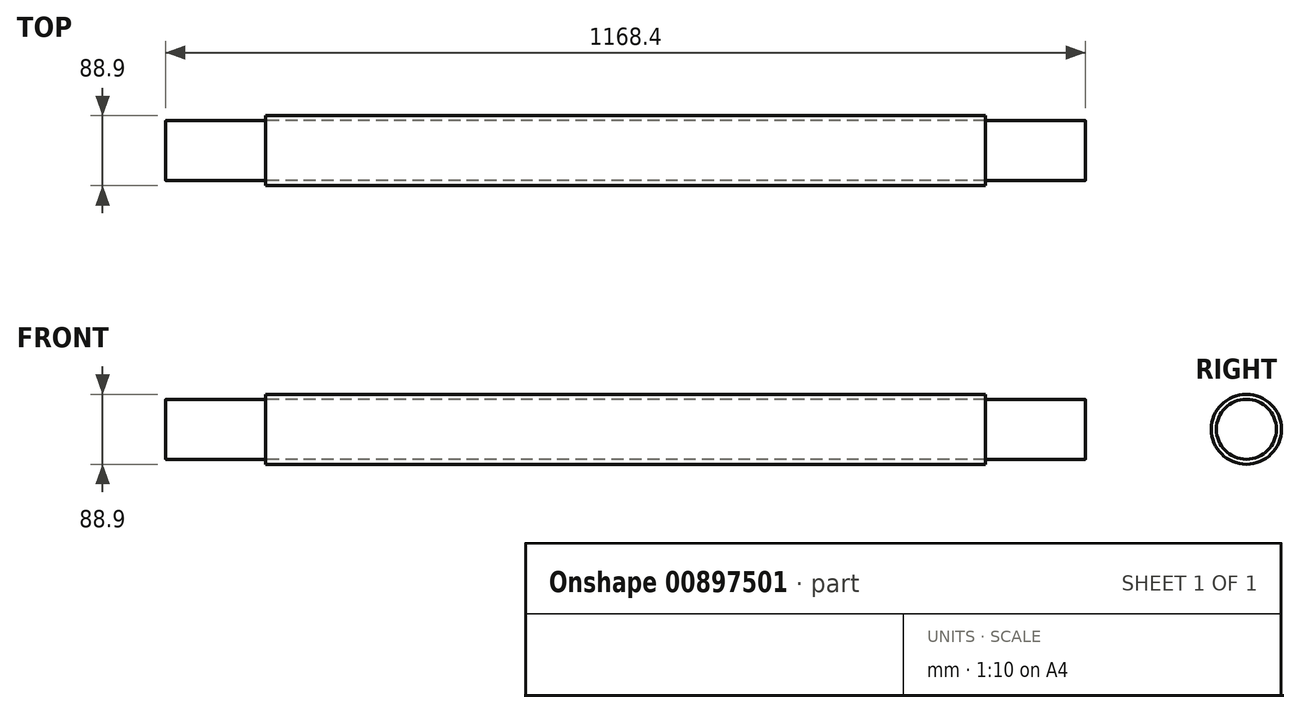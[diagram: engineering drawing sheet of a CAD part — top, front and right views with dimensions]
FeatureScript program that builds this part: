
annotation { "Feature Type Name" : "Feature", "Feature Type Description" : "" }
export const myFeature = defineFeature(function(context is Context, id is Id, definition is map)
    precondition{}
    {
        {
            var Q0;
            Q0=qCreatedBy(makeId("Right.planeOp"),FACE);
            var sketch = newSketch(context, id + "F0", { "sketchPlane" : qUnion([Q0])});
            skCircle(sketch, "E0", {"center": v(0, 0) * mm, "radius": 38.1 * mm});
            skSolve(sketch);
        }
        {
            var Q0;
            Q0=makeQuery(id+"F0.imprint","IMPRINT",FACE,{"disambiguationData":[TD([[makeQuery(id+"F0.imprint","IMPRINT",EDGE,{"derivedFrom":sQuery(id+"F0.wireOp",EDGE,"E0")}),1.0]])]});
            extrude(context, id + "F1", {"entities" : qUnion([Q0]), "endBound" : BoundingType.SYMMETRIC, "depth" : 1168.4 * mm, "offsetDistance" : 25.4 * mm});
        }
        {
            var Q0;
            Q0=makeQuery(id+"F1.opExtrude","CAP_EDGE",EDGE,{"disambiguationData":[OSD([sQuery(id+"F0.wireOp",EDGE,"E0")])],"isStart":true});
            var Q1;
            Q1=makeQuery(id+"F1.opExtrude","CAP_EDGE",EDGE,{"disambiguationData":[OSD([sQuery(id+"F0.wireOp",EDGE,"E0")])],"isStart":false});
            fillet(context, id + "F2", {"entities" : qUnion([Q0, Q1]), "radius" : 0.4 * mm, "tangentPropagation" : true, "allowEdgeOverflow" : false});
        }
        {
            var Q0;
            Q0=qCreatedBy(makeId("Right.planeOp"),FACE);
            var sketch = newSketch(context, id + "F3", { "sketchPlane" : qUnion([Q0])});
            skCircle(sketch, "E1", {"center": v(0, 0) * mm, "radius": 44.45 * mm});
            skSolve(sketch);
        }
        {
            var Q0;
            Q0=makeQuery(id+"F3.imprint","IMPRINT",FACE,{"disambiguationData":[TD([[makeQuery(id+"F3.imprint","IMPRINT",EDGE,{"derivedFrom":sQuery(id+"F3.wireOp",EDGE,"E1")}),1.0]])]});
            extrude(context, id + "F4", {"entities" : qUnion([Q0]), "endBound" : BoundingType.SYMMETRIC, "depth" : 914.4 * mm, "offsetDistance" : 25.4 * mm});
        }
    });
